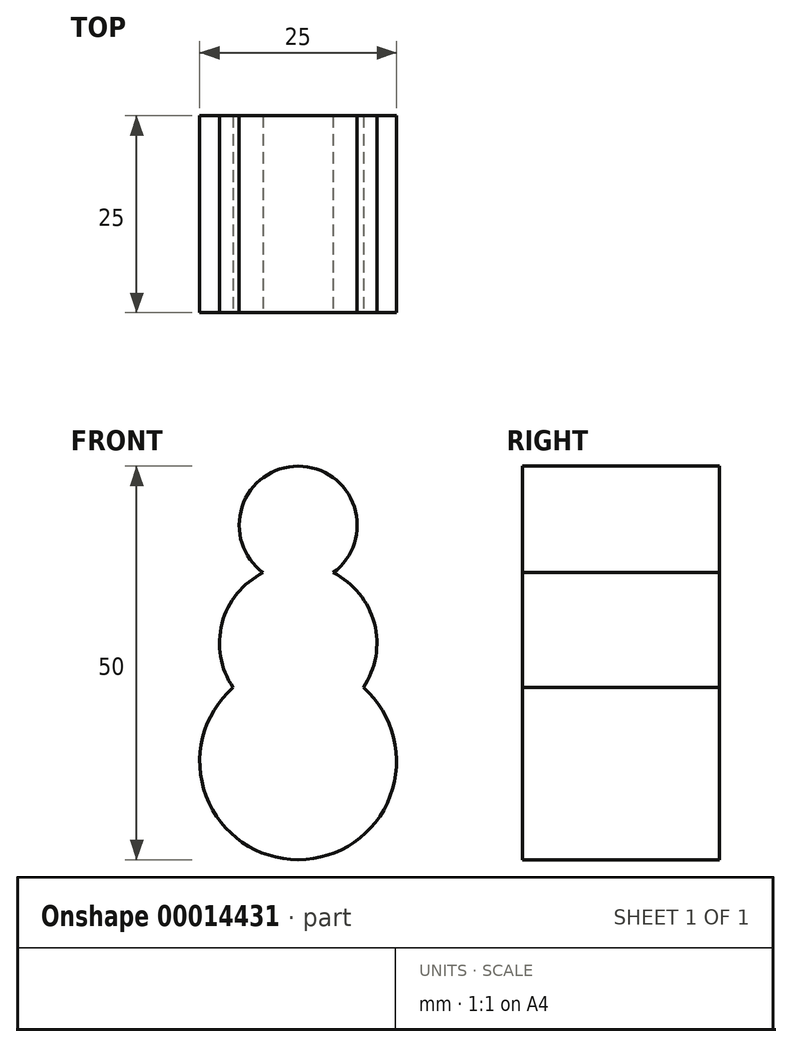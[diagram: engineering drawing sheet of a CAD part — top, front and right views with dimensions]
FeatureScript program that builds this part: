
annotation { "Feature Type Name" : "Feature", "Feature Type Description" : "" }
export const myFeature = defineFeature(function(context is Context, id is Id, definition is map)
    precondition{}
    {
        {
            var Q0;
            Q0=qCreatedBy(makeId("Front.planeOp"),FACE);
            var sketch = newSketch(context, id + "F0", { "sketchPlane" : qUnion([Q0])});
            skArc(sketch, "E0", {"start": v(-4.44, 23.96) * mm, "mid": v(-9.67, 17.54) * mm, "end": v(-8.27, 9.38) * mm});
            skArc(sketch, "E1", {"start": v(-8.27, 9.38) * mm, "mid": v(0, -12.5) * mm, "end": v(8.27, 9.37) * mm});
            skArc(sketch, "E2", {"start": v(4.44, 23.96) * mm, "mid": v(0, 37.5) * mm, "end": v(-4.44, 23.96) * mm});
            skArc(sketch, "E3.trimOffspring", {"start": v(8.27, 9.38) * mm, "mid": v(9.67, 17.54) * mm, "end": v(4.44, 23.96) * mm});
            skSolve(sketch);
        }
        {
            var Q0;
            Q0 = qSketchRegion(id + "F0", true);
            extrude(context, id + "F1", {"entities" : qUnion([Q0]), "endBound" : BoundingType.SYMMETRIC, "oppositeDirection" : true, "depth" : 25 * mm});
        }
    });
